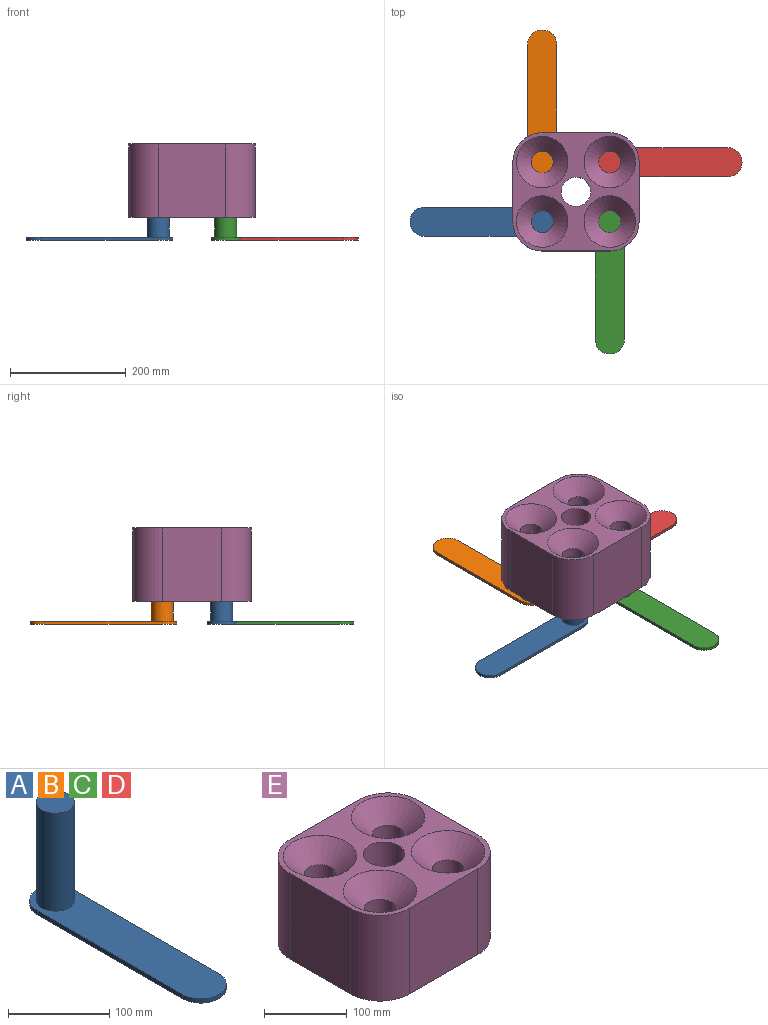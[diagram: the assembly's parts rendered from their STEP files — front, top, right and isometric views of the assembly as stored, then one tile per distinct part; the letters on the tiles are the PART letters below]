
ASSEMBLY  parts=5 mates=4
PART A: 8 faces, bbox 50.8x254x123.7 mm
  f0: plane 203.2x5.08mm, normal (-1,0,0), area 1032.3mm2, adj f1,f3,f4,f5
  f1: cylinder r=25.4mm len=50.8mm, axis (0,0,-1), area 405.4mm2, adj f0,f2,f4,f5
  f2: plane 203.2x5.08mm, normal (1,0,0), area 1032.3mm2, adj f1,f3,f4,f5
  f3: cylinder r=25.4mm len=50.8mm, axis (0,0,-1), area 405.4mm2, adj f0,f2,f4,f5
  f4: plane 254x50.8mm, normal (0,0,1), area 11209.3mm2, adj f0,f1,f2,f3,f6
  f5: plane 254x50.8mm, normal (0,0,-1), area 12349.4mm2, adj f0,f1,f2,f3
  f6: cylinder r=19.05mm len=118.62mm, axis (0,0,-1), area 14197.9mm2, adj f4,f7
  f7: plane 38.1x38.1mm, normal (0,0,1), area 1140.1mm2, adj f6
PART B: same geometry as A
PART C: same geometry as A
PART D: same geometry as A
PART E: 23 faces, bbox 218.3x204.4x127 mm
  f0: cylinder r=50.8mm len=127mm, axis (0,0,-1), area 10134.1mm2, adj f1,f2,f3,f4
  f1: plane 127x102.85mm, normal (-1,0,0), area 13061.4mm2, adj f0,f3,f4,f6
  f2: plane 127x116.69mm, normal (0,1,0), area 14819.3mm2, adj f0,f3,f4,f9
  f3: plane 218.29x204.45mm, normal (0,0,1), area 15557.1mm2, adj f0,f1,f2,f6,f7,f9,f10,f12
  f4: plane 218.29x204.45mm, normal (0,0,-1), area 15557.1mm2, adj f0,f1,f2,f6,f7,f9,f10,f12
  f5: cylinder r=19.05mm len=76.2mm, axis (0,0,1), area 9120.7mm2, adj f20,f21
  f6: cylinder r=50.8mm len=127mm, axis (0,0,-1), area 10134.1mm2, adj f1,f3,f4,f7
  f7: plane 127x116.69mm, normal (0,-1,0), area 14819.3mm2, adj f3,f4,f6,f12
  f8: cylinder r=19.05mm len=76.2mm, axis (0,0,1), area 9120.7mm2, adj f16,f17
  f9: cylinder r=50.8mm len=127mm, axis (0,0,-1), area 10134.1mm2, adj f2,f3,f4,f10
  f10: plane 127x102.85mm, normal (1,0,0), area 13061.4mm2, adj f3,f4,f9,f12
  f11: cylinder r=19.05mm len=76.2mm, axis (0,0,1), area 9120.7mm2, adj f18,f19
  f12: cylinder r=50.8mm len=127mm, axis (0,0,-1), area 10134.1mm2, adj f3,f4,f7,f10
  f13: cylinder r=19.05mm len=76.2mm, axis (0,0,1), area 9120.7mm2, adj f14,f15
  f14: cone r=19.05mm half-angle=45deg, axis (0,0,1), area 7165.9mm2, adj f3,f13
  f15: cone r=44.45mm half-angle=45deg, axis (0,0,-1), area 7165.9mm2, adj f4,f13
  f16: cone r=44.45mm half-angle=45deg, axis (0,0,1), area 7165.9mm2, adj f3,f8
  f17: cone r=19.05mm half-angle=45deg, axis (0,0,-1), area 7165.9mm2, adj f4,f8
  f18: cone r=44.45mm half-angle=45deg, axis (0,0,1), area 7165.9mm2, adj f3,f11
  f19: cone r=19.05mm half-angle=45deg, axis (0,0,-1), area 7165.9mm2, adj f4,f11
  f20: cone r=19.05mm half-angle=45deg, axis (0,0,1), area 7165.9mm2, adj f3,f5
  f21: cone r=44.45mm half-angle=45deg, axis (0,0,-1), area 7165.9mm2, adj f4,f5
  f22: cylinder r=25.4mm len=127mm, axis (0,0,1), area 20268.3mm2, adj f3,f4
PLACE A rot(axis=(0,0,-1),90deg) t=(-14.67,121,-152.94)mm
PLACE B rot(axis=(0,0,1),180deg) t=(-14.67,223.85,-152.94)mm
PLACE C t=(102.02,121,-152.94)mm
PLACE D rot(axis=(0,0,1),90deg) t=(102.02,223.85,-152.94)mm
PLACE E t=(-10.9,223.54,-113.96)mm
MATE revolute A.f3 <-> E.f6  axis (0,0,-1) through (-14.67,121,-88.56)mm
MATE revolute B.f3 <-> E.f0  axis (0,0,-1) through (-14.67,223.85,-88.56)mm
MATE revolute D.f3 <-> E.f9  axis (0,0,-1) through (102.02,223.85,-88.56)mm
MATE revolute C.f3 <-> E.f12  axis (0,0,-1) through (102.02,121,-88.56)mm
